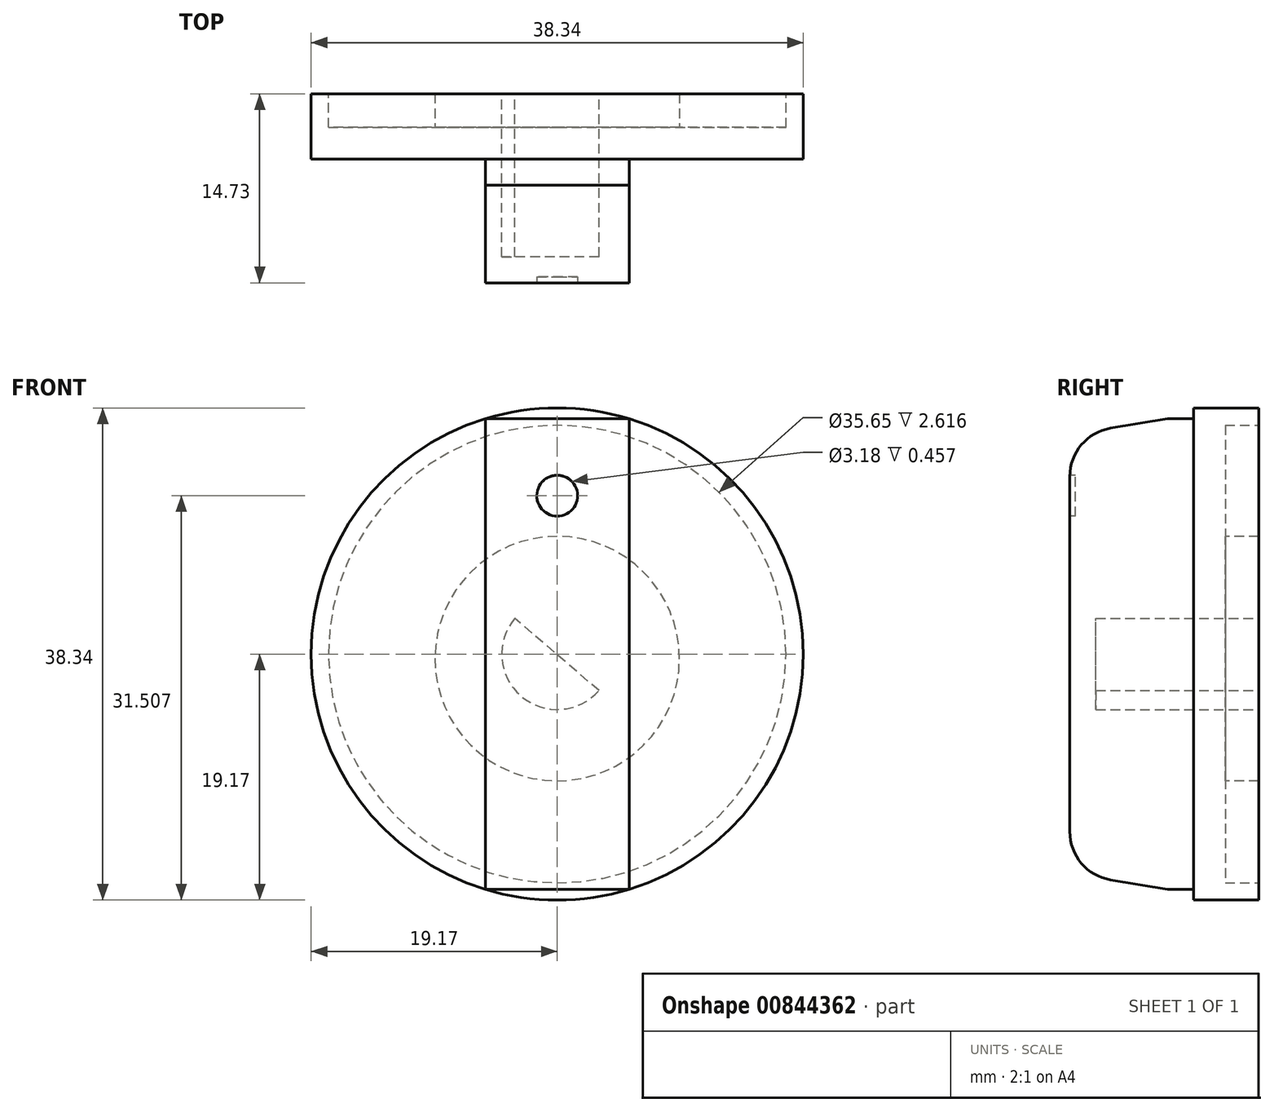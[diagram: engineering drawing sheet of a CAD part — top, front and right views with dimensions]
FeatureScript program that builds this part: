
annotation { "Feature Type Name" : "Feature", "Feature Type Description" : "" }
export const myFeature = defineFeature(function(context is Context, id is Id, definition is map)
    precondition{}
    {
        {
            var Q0;
            Q0=qCreatedBy(makeId("Front.planeOp"),FACE);
            var sketch = newSketch(context, id + "F0", { "sketchPlane" : qUnion([Q0])});
            skCircle(sketch, "E0", {"center": v(0, 0) * mm, "radius": 19.17 * mm});
            skSolve(sketch);
        }
        {
            var Q0;
            Q0=makeQuery(id+"F0.imprint","IMPRINT",FACE,{"disambiguationData":[TD([[makeQuery(id+"F0.imprint","IMPRINT",EDGE,{"derivedFrom":sQuery(id+"F0.wireOp",EDGE,"E0")}),1.0]])]});
            extrude(context, id + "F1", {"entities" : qUnion([Q0]), "depth" : 5.08 * mm, "offsetDistance" : 25.4 * mm});
        }
        {
            var Q0;
            Q0=makeQuery(id+"F1.opExtrude","CAP_FACE",FACE,{"disambiguationData":[OSD([sQuery(id+"F0.wireOp",EDGE,"E0")])],"isStart":true});
            var sketch = newSketch(context, id + "F2", { "sketchPlane" : qUnion([Q0])});
            skCircle(sketch, "E1", {"center": v(0, 0) * mm, "radius": 17.82 * mm});
            skSolve(sketch);
        }
        {
            var Q0;
            Q0=makeQuery(id+"F2.imprint","IMPRINT",FACE,{"disambiguationData":[TD([[makeQuery(id+"F2.imprint","IMPRINT",EDGE,{"derivedFrom":sQuery(id+"F2.wireOp",EDGE,"E1")}),1.0]])]});
            extrude(context, id + "F3", {"entities" : qUnion([Q0]), "operationType" : NewBodyOperationType.REMOVE, "oppositeDirection" : true, "depth" : 2.62 * mm, "offsetDistance" : 25.4 * mm});
        }
        {
            var Q0;
            Q0=makeQuery(id+"F1.opExtrude","CAP_FACE",FACE,{"disambiguationData":[OSD([sQuery(id+"F0.wireOp",EDGE,"E0")])],"isStart":false});
            var sketch = newSketch(context, id + "F4", { "sketchPlane" : qUnion([Q0])});
            skLineSegment(sketch, "E2.bottom", {"start": v(5.6, 18.33) * mm, "end": v(-5.6, 18.33) * mm});
            skLineSegment(sketch, "E2.top", {"start": v(5.6, -18.33) * mm, "end": v(-5.6, -18.33) * mm});
            skLineSegment(sketch, "E2.left", {"start": v(5.6, 18.33) * mm, "end": v(5.6, -18.33) * mm});
            skLineSegment(sketch, "E2.right", {"start": v(-5.6, 18.33) * mm, "end": v(-5.6, -18.33) * mm});
            skPoint(sketch, "E2.middle", {"position": v(0, 0) * mm});
            skSolve(sketch);
        }
        {
            var Q0;
            Q0=makeQuery(id+"F4.imprint","IMPRINT",FACE,{"disambiguationData":[TD([[makeQuery(id+"F4.imprint","IMPRINT",EDGE,{"derivedFrom":sQuery(id+"F4.wireOp",EDGE,"E2.bottom")}),1.0]])]});
            extrude(context, id + "F5", {"entities" : qUnion([Q0]), "operationType" : NewBodyOperationType.ADD, "depth" : 9.65 * mm, "offsetDistance" : 25.4 * mm});
        }
        {
            var Q0;
            Q0=makeQuery(id+"F5.opExtrude","CAP_EDGE",EDGE,{"disambiguationData":[OSD([sQuery(id+"F4.wireOp",EDGE,"E2.bottom")])],"isStart":false});
            var Q1;
            Q1=makeQuery(id+"F5.opExtrude","CAP_EDGE",EDGE,{"disambiguationData":[OSD([sQuery(id+"F4.wireOp",EDGE,"E2.top")])],"isStart":false});
            chamfer(context, id + "F6", {"entities" : qUnion([Q0, Q1]), "chamferType" : ChamferType.TWO_OFFSETS, "width1" : 1.27 * mm, "oppositeDirection" : false, "width2" : 7.62 * mm, "tangentPropagation" : true});
        }
        {
            var Q0;
            {var subQ0=sQuery(id+"F4.wireOp",EDGE,"E2.bottom");Q0=makeQuery(id+"F6.opChamfer","BLEND_EDGE",EDGE,{"blendedFrom":[makeQuery(id+"F5.opExtrude","CAP_EDGE",EDGE,{"disambiguationData":[OSD([subQ0])],"isStart":false}),makeQuery(id+"F5.opExtrude","CAP_FACE",FACE,{"disambiguationData":[OSD([subQ0,sQuery(id+"F4.wireOp",EDGE,"E2.top"),sQuery(id+"F4.wireOp",EDGE,"E2.left"),sQuery(id+"F4.wireOp",EDGE,"E2.right")])],"isStart":false})],"blendedInto":[makeQuery(id+"F5.opExtrude","CAP_FACE",FACE,{"disambiguationData":[OSD([subQ0,sQuery(id+"F4.wireOp",EDGE,"E2.top"),sQuery(id+"F4.wireOp",EDGE,"E2.left"),sQuery(id+"F4.wireOp",EDGE,"E2.right")])],"isStart":false})]});}
            var Q1;
            {var subQ0=sQuery(id+"F4.wireOp",EDGE,"E2.top");Q1=makeQuery(id+"F6.opChamfer","BLEND_EDGE",EDGE,{"blendedFrom":[makeQuery(id+"F5.opExtrude","CAP_EDGE",EDGE,{"disambiguationData":[OSD([subQ0])],"isStart":false}),makeQuery(id+"F5.opExtrude","CAP_FACE",FACE,{"disambiguationData":[OSD([sQuery(id+"F4.wireOp",EDGE,"E2.bottom"),subQ0,sQuery(id+"F4.wireOp",EDGE,"E2.left"),sQuery(id+"F4.wireOp",EDGE,"E2.right")])],"isStart":false})],"blendedInto":[makeQuery(id+"F5.opExtrude","CAP_FACE",FACE,{"disambiguationData":[OSD([sQuery(id+"F4.wireOp",EDGE,"E2.bottom"),subQ0,sQuery(id+"F4.wireOp",EDGE,"E2.left"),sQuery(id+"F4.wireOp",EDGE,"E2.right")])],"isStart":false})]});}
            fillet(context, id + "F7", {"entities" : qUnion([Q0, Q1]), "radius" : 3.8 * mm, "tangentPropagation" : true, "allowEdgeOverflow" : false});
        }
        {
            var Q0;
            Q0=makeQuery(id+"F3.boolean.opBoolean","COPY",FACE,{"derivedFrom":makeQuery(id+"F3.opExtrude","CAP_FACE",FACE,{"disambiguationData":[OSD([sQuery(id+"F2.wireOp",EDGE,"E1")])],"isStart":false})});
            var sketch = newSketch(context, id + "F8", { "sketchPlane" : qUnion([Q0])});
            skCircle(sketch, "E3", {"center": v(0, -0.36) * mm, "radius": 9.52 * mm});
            skSolve(sketch);
        }
        {
            var Q0;
            Q0=makeQuery(id+"F8.imprint","IMPRINT",FACE,{"disambiguationData":[TD([[makeQuery(id+"F8.imprint","IMPRINT",EDGE,{"derivedFrom":sQuery(id+"F8.wireOp",EDGE,"E3")}),1.0]])]});
            var Q1;
            Q1=qCreatedBy(makeId("Origin.pointOp"),VERTEX);
            extrude(context, id + "F9", {"entities" : qUnion([Q0]), "operationType" : NewBodyOperationType.ADD, "endBound" : BoundingType.UP_TO_VERTEX, "depth" : 3.91 * mm, "endBoundEntityVertex" : qUnion([Q1]), "offsetDistance" : 25.4 * mm});
        }
        {
            var Q0;
            Q0=makeQuery(id+"F9.opExtrude","CAP_FACE",FACE,{"disambiguationData":[OSD([sQuery(id+"F8.wireOp",EDGE,"E3")])],"isStart":false});
            var sketch = newSketch(context, id + "F10", { "sketchPlane" : qUnion([Q0])});
            skCircle(sketch, "E4", {"center": v(0, 0) * mm, "radius": 4.32 * mm});
            skLineSegment(sketch, "E5", {"start": v(-3.25, -2.85) * mm, "end": v(3.3, 2.79) * mm});
            skSolve(sketch);
        }
        {
            var Q0;
            {var subQ0=sQuery(id+"F10.wireOp",EDGE,"E5");Q0=makeQuery(id+"F10.imprint","IMPRINT",FACE,{"disambiguationData":[TD([[makeQuery(id+"F10.imprint","IMPRINT",EDGE,{"derivedFrom":subQ0}),-1.0]])]});}
            extrude(context, id + "F11", {"entities" : qUnion([Q0]), "operationType" : NewBodyOperationType.REMOVE, "oppositeDirection" : true, "depth" : 12.7 * mm, "offsetDistance" : 25.4 * mm});
        }
        {
            var Q0;
            Q0=makeQuery(id+"F5.opExtrude","CAP_FACE",FACE,{"disambiguationData":[OSD([sQuery(id+"F4.wireOp",EDGE,"E2.bottom"),sQuery(id+"F4.wireOp",EDGE,"E2.top"),sQuery(id+"F4.wireOp",EDGE,"E2.left"),sQuery(id+"F4.wireOp",EDGE,"E2.right")])],"isStart":false});
            var sketch = newSketch(context, id + "F12", { "sketchPlane" : qUnion([Q0])});
            skCircle(sketch, "E6", {"center": v(0, 12.34) * mm, "radius": 1.6 * mm});
            skSolve(sketch);
        }
        {
            var Q0;
            Q0=makeQuery(id+"F12.imprint","IMPRINT",FACE,{"disambiguationData":[TD([[makeQuery(id+"F12.imprint","IMPRINT",EDGE,{"derivedFrom":sQuery(id+"F12.wireOp",EDGE,"E6")}),1.0]])]});
            extrude(context, id + "F13", {"entities" : qUnion([Q0]), "operationType" : NewBodyOperationType.REMOVE, "oppositeDirection" : true, "depth" : 0.46 * mm, "offsetDistance" : 25.4 * mm});
        }
    });
